# Revit family: НЕВАТОМ_Охладитель OWP-L_20220407
name_source: partatom
category: Оборудование
revit_build: Autodesk Revit 2017 (Build: 20170118_1100(x64)
units: mm (PartAtom-declared; Revit-internal decimal feet)

## family parameters
Всегда вертикально = Нет
На основе рабочей плоскости = Нет
Общий = Нет
При загрузке вырезать с полостями = Нет
Размер круглого соединителя = Использовать диаметр
Тип детали = Вставляется
Точка расчета площади = Нет

## types (27) — shared parameters
312 = 312 мм
5 = 5 мм
ADSK_Единица измерения = шт.
ADSK_Завод-изготовитель = NEVATOM
ADSK_Материал наименование = Оцинкованная сталь
ADSK_Наименование = ОХЛАДИТЕЛЬ ВОДЯНОЙ
ADSK_Напряжение = 0 В
ADSK_Полная мощность = 0 кВт
ADSK_Размер_Ширина = 312 мм
ADSK_Ток = 0 А
F = 43 мм
Nevatom_URL = https://t.me
d = 20 мм
l = 30 мм
t = 2 мм
Материал корпуса = Материал корпуса
Толщина крышки = 50 мм

## per-type parameters (varying)
| type | A | ADSK_Марка | ADSK_Масса | ADSK_Масса_Текст | ADSK_Потеря давления воздуха | ADSK_Размер_Высота | ADSK_Размер_Длина | ADSK_Расход воздуха | B | C | D | D пр.сеч | E | K | N | С пр. сеч |
| OWP 400-200/2 | 556 мм | ОWP–400*200/2-L | 17.7 | 17,7 кг | 31.0 Па | 333 мм | 675 мм | 800.0 м³/ч | 333 мм | 220 мм | 420 мм | 400 мм | 219 мм | 675 мм | 14 | 200 мм |
| OWP 400-200/3 | 556 мм | ОWP–400*200/3-L | 17.7 | 17,7 кг | 47.0 Па | 333 мм | 675 мм | 800.0 м³/ч | 333 мм | 220 мм | 420 мм | 400 мм | 219 мм | 675 мм | 14 | 200 мм |
| OWP 400-200/4 | 556 мм | ОWP–400*200/4-L | 18.7 | 18,7 кг | 67.0 Па | 333 мм | 675 мм | 800.0 м³/ч | 333 мм | 220 мм | 420 мм | 400 мм | 219 мм | 675 мм | 14 | 200 мм |
| OWP 500-250/2 | 656 мм | OWP 500-250/2-L | 21.4 | 21,4 кг | 31.0 Па | 383 мм | 775 мм | 1250.0 м³/ч | 383 мм | 270 мм | 520 мм | 500 мм | 269 мм | 775 мм | 17 | 250 мм |
| OWP 500-250/3 | 656 мм | OWP 500-250/3-L | 21.2 | 21,2 кг | 51.0 Па | 383 мм | 775 мм | 1250.0 м³/ч | 383 мм | 270 мм | 520 мм | 500 мм | 269 мм | 775 мм | 17 | 250 мм |
| OWP 500-250/4 | 656 мм | OWP 500-250/4-L | 23 | 23 кг | 72.0 Па | 383 мм | 775 мм | 1250.0 м³/ч | 383 мм | 270 мм | 520 мм | 500 мм | 269 мм | 775 мм | 17 | 250 мм |
| OWP 500-300/2 | 656 мм | OWP 500-300/2-L | 23.1 | 23,1 кг | 35.0 Па | 433 мм | 775 мм | 1600.0 м³/ч | 433 мм | 320 мм | 520 мм | 500 мм | 319 мм | 775 мм | 17 | 300 мм |
| OWP 500-300/3 | 656 мм | OWP 500-300/3-L | 22.7 | 22,7 кг | 58.0 Па | 433 мм | 775 мм | 1600.0 м³/ч | 433 мм | 320 мм | 520 мм | 500 мм | 319 мм | 775 мм | 17 | 300 мм |
| OWP 500-300/4 | 656 мм | OWP 500-300/4-L | 24.9 | 24,9 кг | 79.0 Па | 433 мм | 775 мм | 1600.0 м³/ч | 433 мм | 320 мм | 520 мм | 500 мм | 319 мм | 775 мм | 17 | 300 мм |
| OWP 600-300/2 | 756 мм | OWP 600-300/2-L | 25.1 | 25,1 кг | 37.0 Па | 433 мм | 875 мм | 1850.0 м³/ч | 433 мм | 320 мм | 620 мм | 600 мм | 319 мм | 875 мм | 21 | 300 мм |
| OWP 600-300/3 | 756 мм | OWP 600-300/3-L | 25.2 | 25,2 кг | 56.0 Па | 433 мм | 875 мм | 1850.0 м³/ч | 433 мм | 320 мм | 620 мм | 600 мм | 319 мм | 875 мм | 21 | 300 мм |
| OWP 600-300/4 | 756 мм | OWP 600-300/4-L | 27.6 | 27,6 кг | 73.0 Па | 433 мм | 875 мм | 1850.0 м³/ч | 433 мм | 320 мм | 620 мм | 600 мм | 319 мм | 875 мм | 21 | 300 мм |
| OWP 600-350/2 | 756 мм | OWP 600-350/2-L | 27 | 27,0 кг | 37.0 Па | 483 мм | 875 мм | 2150.0 м³/ч | 483 мм | 370 мм | 620 мм | 600 мм | 369 мм | 875 мм | 21 | 350 мм |
| OWP 600-350/3 | 756 мм | OWP 600-350/3-L | 26.7 | 26,7 кг | 56.0 Па | 483 мм | 875 мм | 2150.0 м³/ч | 483 мм | 370 мм | 620 мм | 600 мм | 369 мм | 875 мм | 21 | 350 мм |
| OWP 600-350/4 | 756 мм | OWP 600-350/4-L | 29.6 | 29,6 кг | 74.0 Па | 483 мм | 875 мм | 2150.0 м³/ч | 483 мм | 370 мм | 620 мм | 600 мм | 369 мм | 875 мм | 21 | 350 мм |
| OWP 700-400/2 | 856 мм | OWP 700-400/2-L | 31 | 31,0 кг | 55.0 Па | 523 мм | 975 мм | 3500.0 м³/ч | 523 мм | 420 мм | 720 мм | 700 мм | 419 мм | 975 мм | 24 | 400 мм |
| OWP 700-400/3 | 856 мм | OWP 700-400/3-L | 30.6 | 30,6 кг | 80.0 Па | 523 мм | 975 мм | 3500.0 м³/ч | 523 мм | 420 мм | 720 мм | 700 мм | 419 мм | 975 мм | 24 | 400 мм |
| OWP 700-400/4 | 856 мм | OWP 700-400/4-L | 34.6 | 34,6 кг | 104.0 Па | 523 мм | 975 мм | 3500.0 м³/ч | 523 мм | 420 мм | 720 мм | 700 мм | 419 мм | 975 мм | 24 | 400 мм |
| OWP 800-500/2 | 976 мм | OWP 800-500/2-L | 38.2 | 38,2 кг | 56.0 Па | 643 мм | 1095 мм | 5000.0 м³/ч | 643 мм | 530 мм | 830 мм | 800 мм | 519 мм | 1095 мм | 28 | 500 мм |
| OWP 800-500/3 | 976 мм | OWP 800-500/3-L | 37.3 | 37,3 кг | 81.0 Па | 643 мм | 1095 мм | 5000.0 м³/ч | 643 мм | 530 мм | 830 мм | 800 мм | 519 мм | 1095 мм | 28 | 500 мм |
| OWP 800-500/4 | 976 мм | OWP 800-500/4-L | 43.1 | 43,1 кг | 97.0 Па | 643 мм | 1095 мм | 5000.0 м³/ч | 643 мм | 530 мм | 830 мм | 800 мм | 519 мм | 1095 мм | 28 | 500 мм |
| OWP 900-500/2 | 1076 мм | OWP 900-500/2-L | 42.1 | 42,1 кг | 54.0 Па | 643 мм | 1195 мм | 5500.0 м³/ч | 643 мм | 530 мм | 930 мм | 900 мм | 519 мм | 1195 мм | 31 | 500 мм |
| OWP 900-500/3 | 1076 мм | OWP 900-500/3-L | 39.6 | 39,6 кг | 77.0 Па | 643 мм | 1195 мм | 5500.0 м³/ч | 643 мм | 530 мм | 930 мм | 900 мм | 519 мм | 1195 мм | 31 | 500 мм |
| OWP 900-500/4 | 1076 мм | OWP 900-500/4-L | 46.6 | 46,6 кг | 96.0 Па | 643 мм | 1195 мм | 5500.0 м³/ч | 643 мм | 530 мм | 930 мм | 900 мм | 519 мм | 1195 мм | 31 | 500 мм |
| OWP 1000-500/2 | 1176 мм | OWP 1000-500/2-L | 45.2 | 45,2 кг | 54.0 Па | 643 мм | 1295 мм | 6000.0 м³/ч | 643 мм | 530 мм | 1030 мм | 1000 мм | 519 мм | 1295 мм | 34 | 500 мм |
| OWP 1000-500/3 | 1176 мм | OWP 1000-500/3-L | 42.4 | 42,4 кг | 77.0 Па | 643 мм | 1295 мм | 6000.0 м³/ч | 643 мм | 530 мм | 1030 мм | 1000 мм | 519 мм | 1295 мм | 34 | 500 мм |
| OWP 1000-500/4 | 1176 мм | OWP 1000-500/4-L | 49.8 | 49,8 кг | 95.0 Па | 643 мм | 1295 мм | 6000.0 м³/ч | 643 мм | 530 мм | 1030 мм | 1000 мм | 519 мм | 1295 мм | 34 | 500 мм |
